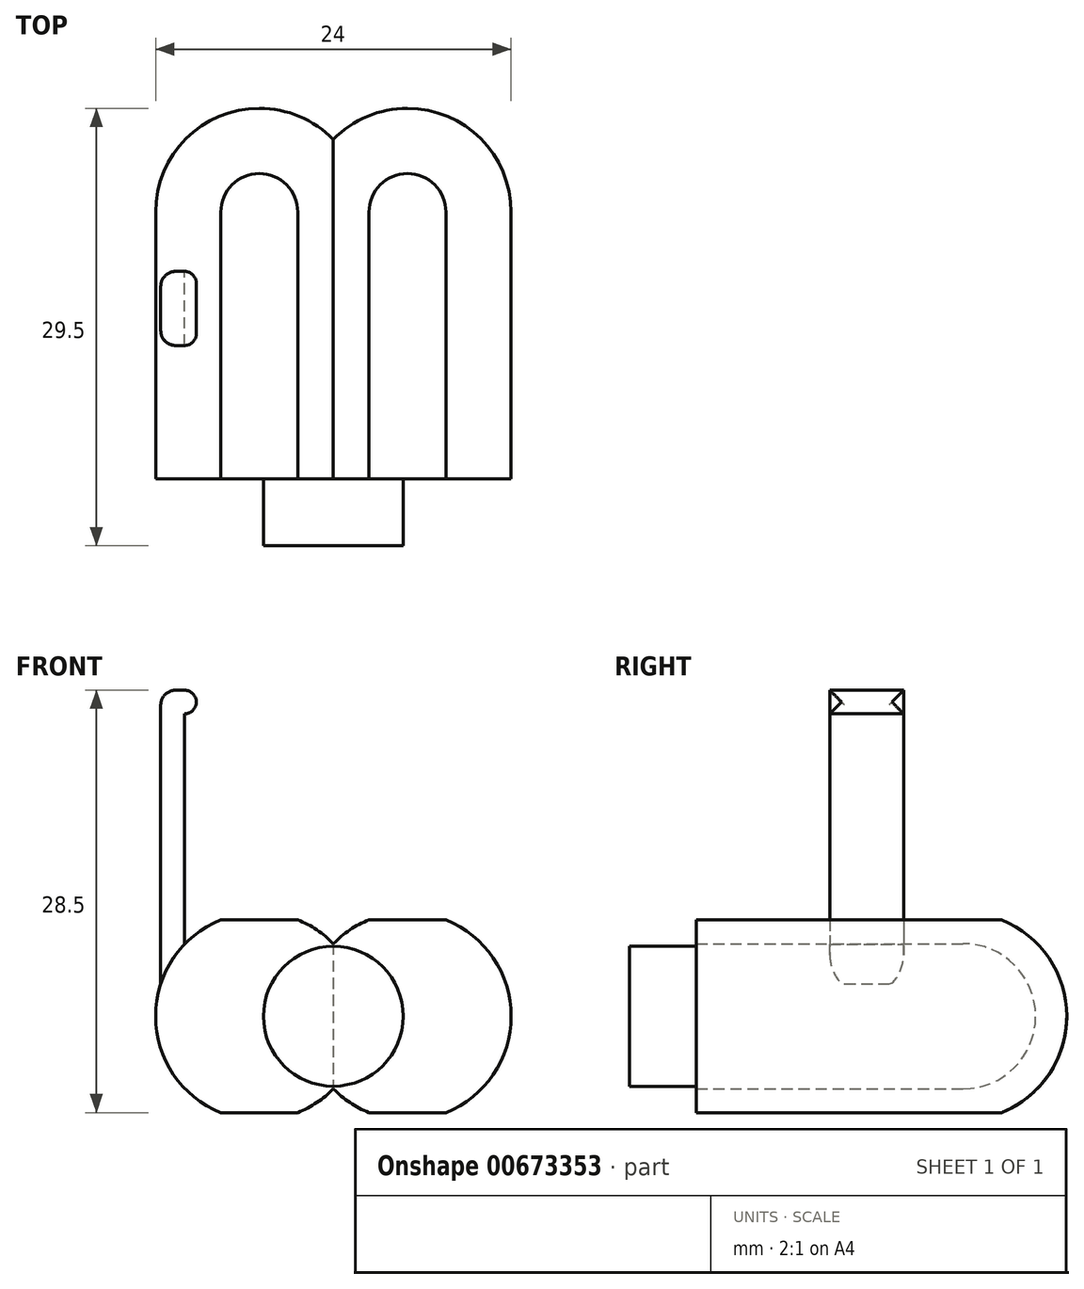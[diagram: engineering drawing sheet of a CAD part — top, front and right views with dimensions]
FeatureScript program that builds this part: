
annotation { "Feature Type Name" : "Feature", "Feature Type Description" : "" }
export const myFeature = defineFeature(function(context is Context, id is Id, definition is map)
    precondition{}
    {
        {
            var Q0;
            Q0=qCreatedBy(makeId("Front.planeOp"),FACE);
            var sketch = newSketch(context, id + "F0", { "sketchPlane" : qUnion([Q0])});
            skCircle(sketch, "E0", {"center": v(0, 0) * mm, "radius": 7 * mm});
            skSolve(sketch);
        }
        {
            var Q0;
            Q0 = qSketchRegion(id + "F0", true);
            extrude(context, id + "F1", {"entities" : qUnion([Q0]), "depth" : 25 * mm, "offsetDistance" : 25 * mm});
        }
        {
            var Q0;
            Q0=makeQuery(id+"F1.opExtrude","CAP_FACE",FACE,{"disambiguationData":[OSD([sQuery(id+"F0.wireOp",EDGE,"E0")])],"isStart":true});
            fillet(context, id + "F2", {"entities" : qUnion([Q0]), "radius" : 7 * mm, "tangentPropagation" : true, "allowEdgeOverflow" : false});
        }
        {
            var Q0;
            Q0=qCreatedBy(makeId("Front.planeOp"),FACE);
            var sketch = newSketch(context, id + "F3", { "sketchPlane" : qUnion([Q0])});
            skCircle(sketch, "E1", {"center": v(10, 0) * mm, "radius": 7 * mm});
            skSolve(sketch);
        }
        {
            var Q0;
            Q0 = qSketchRegion(id + "F3", true);
            extrude(context, id + "F4", {"entities" : qUnion([Q0]), "operationType" : NewBodyOperationType.ADD, "depth" : 25 * mm, "offsetDistance" : 25 * mm});
        }
        {
            var Q0;
            Q0=makeQuery(id+"F4.opExtrude","CAP_FACE",FACE,{"disambiguationData":[OSD([sQuery(id+"F3.wireOp",EDGE,"E1")])],"isStart":true});
            fillet(context, id + "F5", {"entities" : qUnion([Q0]), "radius" : 7 * mm, "tangentPropagation" : true, "allowEdgeOverflow" : false});
        }
        {
            var Q0;
            Q0=qCreatedBy(makeId("Front.planeOp"),FACE);
            var sketch = newSketch(context, id + "F6", { "sketchPlane" : qUnion([Q0])});
            skLineSegment(sketch, "E2.bottom", {"start": v(-9, 8.5) * mm, "end": v(19, 8.5) * mm});
            skLineSegment(sketch, "E2.top", {"start": v(-9, 6.5) * mm, "end": v(19, 6.5) * mm});
            skLineSegment(sketch, "E2.left", {"start": v(-9, 8.5) * mm, "end": v(-9, 6.5) * mm});
            skLineSegment(sketch, "E2.right", {"start": v(19, 8.5) * mm, "end": v(19, 6.5) * mm});
            skLineSegment(sketch, "E3.MirrorCS", {"start": v(-9, -8.5) * mm, "end": v(-9, -6.5) * mm});
            skLineSegment(sketch, "E4.MirrorCS", {"start": v(19, -8.5) * mm, "end": v(19, -6.5) * mm});
            skLineSegment(sketch, "E5.MirrorCS", {"start": v(-9, -6.5) * mm, "end": v(19, -6.5) * mm});
            skLineSegment(sketch, "E6.MirrorCS", {"start": v(-9, -8.5) * mm, "end": v(19, -8.5) * mm});
            skSolve(sketch);
        }
        {
            var Q0;
            Q0 = qSketchRegion(id + "F6", true);
            extrude(context, id + "F7", {"entities" : qUnion([Q0]), "operationType" : NewBodyOperationType.REMOVE, "depth" : 25 * mm, "offsetDistance" : 25 * mm});
        }
        {
            var Q0;
            Q0=makeQuery(id+"F4.boolean.opBoolean","INTERSECT",VERTEX,{"disambiguationData":[OD(1.0)],"derivedFrom":[makeQuery(id+"F1.opExtrude","SWEPT_FACE",FACE,{"disambiguationData":[OSD([sQuery(id+"F0.wireOp",EDGE,"E0")])]}),makeQuery(id+"F4.opExtrude","SWEPT_FACE",FACE,{"disambiguationData":[OSD([sQuery(id+"F3.wireOp",EDGE,"E1")])]})]});
            var Q1;
            Q1=makeQuery(id+"F4.boolean.opBoolean","INTERSECT",VERTEX,{"disambiguationData":[OD(0.0)],"derivedFrom":[makeQuery(id+"F1.opExtrude","SWEPT_FACE",FACE,{"disambiguationData":[OSD([sQuery(id+"F0.wireOp",EDGE,"E0")])]}),makeQuery(id+"F4.opExtrude","SWEPT_FACE",FACE,{"disambiguationData":[OSD([sQuery(id+"F3.wireOp",EDGE,"E1")])]})]});
            var Q2;
            {var subQ0=sQuery(id+"F3.wireOp",EDGE,"E1");var subQ1=sQuery(id+"F0.wireOp",EDGE,"E0");Q2=makeQuery(id+"F5.opFillet","BLEND_VERTEX",VERTEX,{"disambiguationData":[OD(1.0)],"blendedFrom":[makeQuery(id+"F4.opExtrude","CAP_EDGE",EDGE,{"disambiguationData":[OSD([subQ0])],"isStart":true}),makeQuery(id+"F2.opFillet","BLEND_FACE",FACE,{"disambiguationData":[OSD([subQ1])]}),makeQuery(id+"F1.opExtrude","SWEPT_FACE",FACE,{"disambiguationData":[OSD([subQ1])]}),makeQuery(id+"F4.opExtrude","SWEPT_FACE",FACE,{"disambiguationData":[OSD([subQ0])]})],"blendedInto":[makeQuery(id+"F2.opFillet","BLEND_FACE",FACE,{"disambiguationData":[OSD([subQ1])]}),makeQuery(id+"F1.opExtrude","SWEPT_FACE",FACE,{"disambiguationData":[OSD([subQ1])]}),makeQuery(id+"F4.opExtrude","SWEPT_FACE",FACE,{"disambiguationData":[OSD([subQ0])]})]});}
            cPlane(context, id + "F8", {"entities" : qUnion([Q0, Q1, Q2]), "cplaneType" : CPlaneType.THREE_POINT, "offset" : 0 * mm, "width" : 150 * mm, "height" : 150 * mm});
        }
        {
            var Q0;
            Q0=qCreatedBy(makeId("Top.planeOp"),FACE);
            var sketch = newSketch(context, id + "F9", { "sketchPlane" : qUnion([Q0])});
            skLineSegment(sketch, "E7.bottom", {"start": v(-6.65, -16) * mm, "end": v(-5.05, -16) * mm});
            skLineSegment(sketch, "E7.top", {"start": v(-6.65, -11) * mm, "end": v(-5.05, -11) * mm});
            skLineSegment(sketch, "E7.left", {"start": v(-6.65, -16) * mm, "end": v(-6.65, -11) * mm});
            skLineSegment(sketch, "E7.right", {"start": v(-5.05, -16) * mm, "end": v(-5.05, -11) * mm});
            skSolve(sketch);
        }
        {
            var Q0;
            Q0 = qSketchRegion(id + "F9", true);
            extrude(context, id + "F10", {"entities" : qUnion([Q0]), "operationType" : NewBodyOperationType.ADD, "depth" : 22 * mm, "offsetDistance" : 25 * mm});
        }
        {
            var Q0;
            Q0=makeQuery(id+"F10.opExtrude","SWEPT_EDGE",EDGE,{"disambiguationData":[OSD([sQuery(id+"F9.wireOp",EDGE,"E7.bottom"),sQuery(id+"F9.wireOp",EDGE,"E7.left")])]});
            var Q1;
            Q1=makeQuery(id+"F10.opExtrude","SWEPT_EDGE",EDGE,{"disambiguationData":[OSD([sQuery(id+"F9.wireOp",EDGE,"E7.top"),sQuery(id+"F9.wireOp",EDGE,"E7.left")])]});
            var Q2;
            Q2=makeQuery(id+"F10.opExtrude","CAP_EDGE",EDGE,{"disambiguationData":[OSD([sQuery(id+"F9.wireOp",EDGE,"E7.left")])],"isStart":false});
            fillet(context, id + "F11", {"entities" : qUnion([Q0, Q1, Q2]), "radius" : 1 * mm, "allowEdgeOverflow" : false});
        }
        {
            var Q0;
            Q0=makeQuery(id+"F10.opExtrude","SWEPT_FACE",FACE,{"disambiguationData":[OSD([sQuery(id+"F9.wireOp",EDGE,"E7.right")])]});
            var sketch = newSketch(context, id + "F12", { "sketchPlane" : qUnion([Q0])});
            skLineSegment(sketch, "E8.bottom", {"start": v(-16, 22) * mm, "end": v(-11, 22) * mm});
            skLineSegment(sketch, "E8.top", {"start": v(-16, 20.4) * mm, "end": v(-11, 20.4) * mm});
            skLineSegment(sketch, "E8.left", {"start": v(-16, 22) * mm, "end": v(-16, 20.4) * mm});
            skLineSegment(sketch, "E8.right", {"start": v(-11, 22) * mm, "end": v(-11, 20.4) * mm});
            skSolve(sketch);
        }
        {
            var Q0;
            Q0 = qSketchRegion(id + "F12", true);
            extrude(context, id + "F13", {"entities" : qUnion([Q0]), "operationType" : NewBodyOperationType.ADD, "depth" : .8 * mm, "offsetDistance" : 25 * mm});
        }
        {
            var Q0;
            Q0=makeQuery(id+"F13.opExtrude","CAP_FACE",FACE,{"disambiguationData":[OSD([sQuery(id+"F12.wireOp",EDGE,"E8.bottom"),sQuery(id+"F12.wireOp",EDGE,"E8.top"),sQuery(id+"F12.wireOp",EDGE,"E8.left"),sQuery(id+"F12.wireOp",EDGE,"E8.right")])],"isStart":false});
            fillet(context, id + "F14", {"entities" : qUnion([Q0]), "radius" : .8 * mm, "tangentPropagation" : true, "allowEdgeOverflow" : false});
        }
        {
            var Q0;
            Q0=makeQuery(id+"F4.boolean.opBoolean","MERGE",FACE,{"derivedFrom":[makeQuery(id+"F1.opExtrude","CAP_FACE",FACE,{"disambiguationData":[OSD([sQuery(id+"F0.wireOp",EDGE,"E0")])],"isStart":false}),makeQuery(id+"F4.opExtrude","CAP_FACE",FACE,{"disambiguationData":[OSD([sQuery(id+"F3.wireOp",EDGE,"E1")])],"isStart":false})]});
            var sketch = newSketch(context, id + "F15", { "sketchPlane" : qUnion([Q0])});
            skCircle(sketch, "E9", {"center": v(5, 0) * mm, "radius": 4.72 * mm});
            skSolve(sketch);
        }
        {
            var Q0;
            Q0 = qSketchRegion(id + "F15", true);
            extrude(context, id + "F16", {"entities" : qUnion([Q0]), "operationType" : NewBodyOperationType.ADD, "depth" : 4.5 * mm, "offsetDistance" : 25 * mm});
        }
    });
